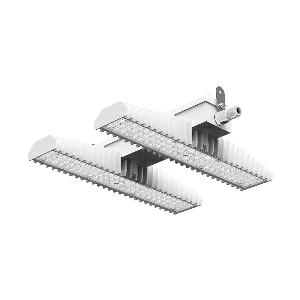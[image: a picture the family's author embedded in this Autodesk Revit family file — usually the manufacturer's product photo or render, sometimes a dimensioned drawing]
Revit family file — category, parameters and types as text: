
# Revit family: 3f_filippi_-_3f_lem_concentrato_3f_filippi_-_58906_-_3f_lem_2_led_100_dali_cr_conc
name_source: partatom
category: Lighting Fixtures
units: mm (PartAtom-declared; Revit-internal decimal feet)

## family parameters
Cut with Voids When Loaded = No
Host = Face
Light Source = No
Part Type = Normal
Room Calculation Point = No
Round Connector Dimension = Use Diameter
Shared = No

## types (1)
- 3F Filippi - 3F LEM Concentrato (1 x LED, 16270 lm, 109 W, 4000 K)
    Apparent Load = 109 VA
    Approval mark = CE
    CIE Flux Codes = 83 96 99 100 100
    Color Rendering = 80
    Color Temperature = 4000 K
    Control Gear = Electronic transformer
    Default Elevation = 1800 mm
    Description = Industrial luminaire with high light output and high luminous efficiency designed with the most innovative technologies for environments with temperature up to 55°C.

ILLUMINOTECHNICAL
Luminous efficiency 100% (DLOR 100%, ULOR 0%).
Initial luminous flux of the luminaire 16270 lm.
Direct symmetric narrow distribution: the illuminated area has a elliptical shape.
Installation Interdistance Transv.D = 0.52 x hu - Long.D = 1.16 x hu.
Tabular UGR (CIE 117 - 4H-8H; S=0.25H; 70/50/20): RUG 16.8 - 20.6.
Beam angle: 31° - 73°.
Luminous efficacy 149 lm/W.
Lifetime (L93/B10): 30000 h. (tq+25°C)
Lifetime (L90/B10): 50000 h. (tq+25°C)
Lifetime (L85/B10): 80000 h. (tq+25°C)
Lifetime (L80/B10): 100000 h. (tq+25°C)
Lifetime (L85/B10): 50000 h. (tq+55°C)
Sudden decreased luminous flux after 50000 hours: 0% (C0).
Photobiological safety in compliance with IEC/TR 62778: RG0 risk exempt, (IEC 62471).
In compliance with IEC/EN 62722-2-1 - IEC/EN 62717 standards.

SOURCE
2 Mid-Power linear LED modules 50W/840.
Energy efficiency class (UE 2019/2020 - UE 2019/2015): C.
CIE 13.3 Colour rendering index: CRI >80 (R9 <50%).
IES TM-30 Fidelity Index: Rf = 84 Rg = 95.
CCT nominal colour temperature 4000 K.
Colour initial tolerance (MacAdam): SDCM 3.

MECHANICAL
Passive modular heatsinks in die-casted aluminium, painted in white colour.
To optimize the thermal management of the LED module, the heatsinks are oversized and provided with self-cleaning of cooling fins.
Wiring body in aluminium and galvanised steel anchored solidly to the sinks and thermally separated.
3F Lens lenses with high luminous efficiency, transparent methacrylate (PMMA), fixed to the LED modules.
Fixing brackets in stainless steel.
Luminaire with limited surface temperature. - D - (EN 60598-2-24)
Dimensions: 470x542 mm, height 129 mm. Weight 9.135 kg.
IP65 protection degree.
Mechanical strength to impacts IK06 (1 joule).
Glow-wire test resistance 650°C.

ELECTRICAL
Halogen Free DALI-2 DATI (Parts 251, 252, 253), PUSH-DIM, electronic wiring 230V-50/60Hz, power factor 0.97 at full load, THD <25%, constant output current, class I, 1 driver, 1 DALI addresse.
Power of the luminaire 109 W.
ENEC - CE.
Flicker: <4%.
Luminaire compliant with EN 60598-2-22 for power supply from a centralised emergency system CPSS (Central Power Supply System), not incorporated in the luminaire - high risk areas excluded. The default power and flux are 100% in AC and 15% in DC.
Ambient temperature from -30°C to +55°C.
Temperature class T6 max 85°C.
Quick connection via M25 5P connector with 9-13 mm tightening range.
Power unit positioned on a separate compartment by the LED module to ensure optimum temperatures of cabling components, to be inspectable and maintainable.
Relative humidity UR: <85%.

INSTALLATION
Ceiling / Suspended / Wall.
All accessories dedicated to this product are available on the Catalog and on our website www.3F-Filippi.com.

APPLICATIONS
In commercial environments, exhibition and industrial areas, stores, open areas.
Applications with high ambient temperature up to 55°C.
Environments in which it is necessary a total protection against falling fragments (eg environments with foodstuffs or machines with moving parts or with extreme temperature changes), use luminaires with polycarbonate lenses.

LIGHT MANAGEMENT
Recommended minimum setting: 10%.
The luminaire, equipped with (DALI-2 DATI) driver, can be controlled manually with 3F Easy Dim technology or automatically/manually with wired or wireless DALI/D2D control systems.
The D2D driver guarantees interoperability with other devices with the same certification by making the following information available:
Device Data (Part 251), Energy Report (Part 252), Diagnosis & Maintenance (Part 253).
In electrical systems without a regulation system (manual or automatic) and DALI bus, a suitable jumper must be made on the DA-DA terminals of the appliance.

WARNING
Fixture not suitable for cold stores with an ambient temperature <0°C and/or relative humidity >85%.
Luminaire designed for disposal/recycling at end-of-life.
Replaceable (LED only) light source by a professional. Replaceable control gear by a professional.
    Height = 129 mm
    Lamp = 1 x LED
    Lamp Light Flux = 16270 lm
    Lamp Power = 109 W
    Lamp count = 1
    Length = 470 mm
    Lifetime = 50000 h
    Luminous efficacy = 149 lm/W
    Manufacturer = 3F Filippi
    ModVariant = No
    Model = 3F Filippi - 58906 - 3F LEM 2 LED 100 DALI CR CONC
    Mounting Place = Ceiling
    Mounting Type = Pendant
    Number of Poles = 1
    OnlyDefault = Yes
    Power Factor = 1
    Product Name = 3F Filippi - 3F LEM Concentrato
    Product group = pendant luminaire
    ProductGroupID = 9
    Protection Class = Protection class I
    Protection Degree = IP 65
    RLX_Detail_Level = 1
    RLX_Emergency_Light_Flux = 0 lm
    RLX_Emergency_Type = 0
    RLX_Emergency_Type_DB = No
    RlxData = <blob elided: 98661 chars, md5=68c01d71>
    Socket = socket
    Standby Power = 0 W
    System Light Flux = 16270 lm
    System Power = 109 W
    Type Comments = Product without accessories
    Type Image = 3f_filippi_-_lem_2.jpg
    URL = http://relux.com
    VarID = ---
    Voltage = 0 V
    Weight = 0.00 kg
    Width = 542 mm

## geometry (parser evidence)
native form markers: Blend x4, Sweep x12
no freeform markers — native parametric forms only
